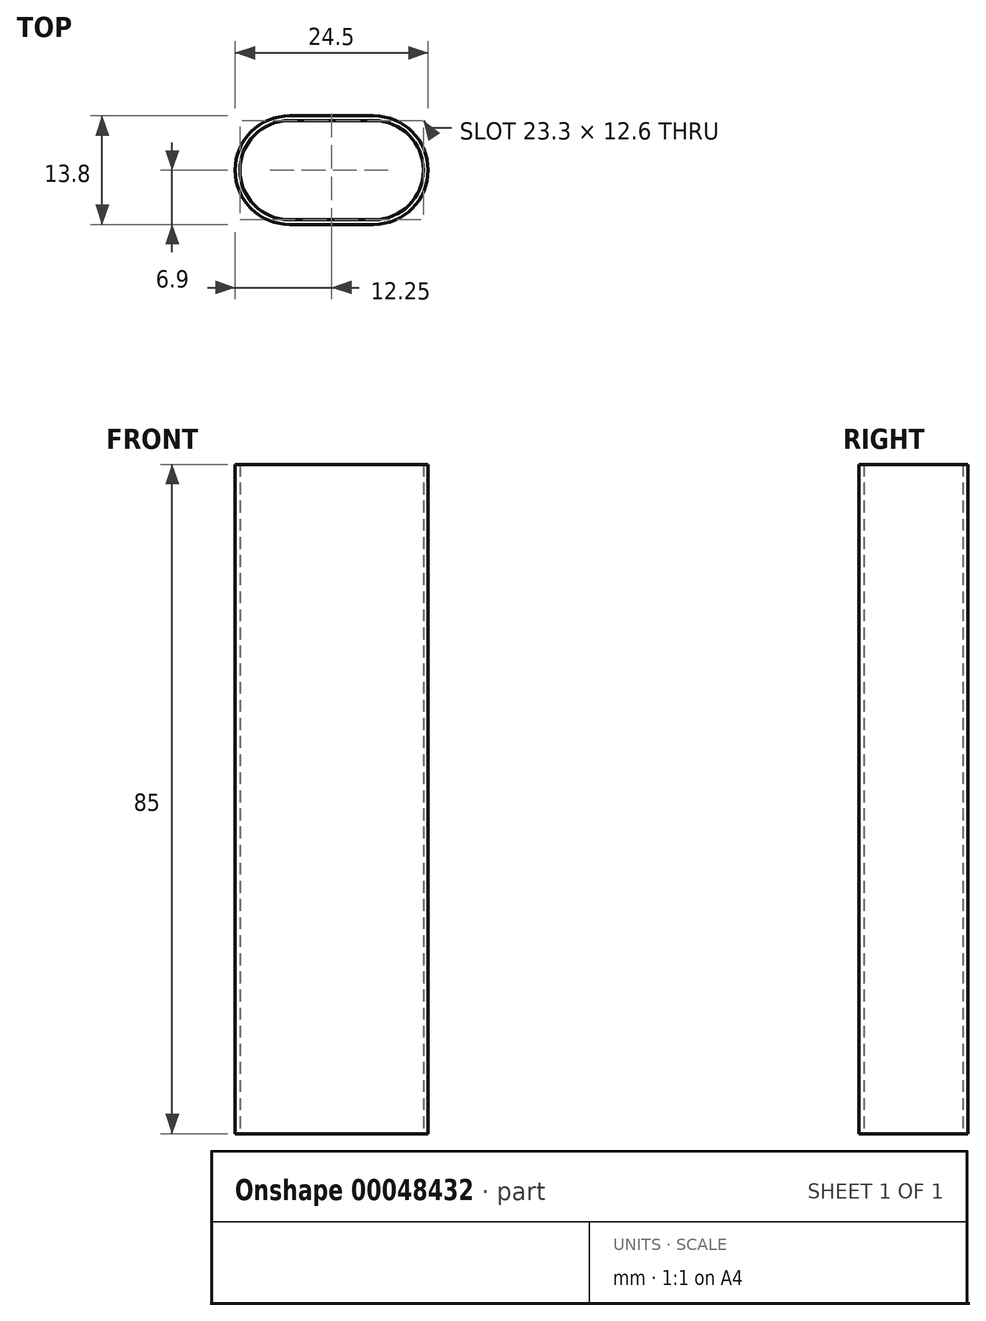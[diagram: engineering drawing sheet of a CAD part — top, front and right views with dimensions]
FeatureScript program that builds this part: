
annotation { "Feature Type Name" : "Feature", "Feature Type Description" : "" }
export const myFeature = defineFeature(function(context is Context, id is Id, definition is map)
    precondition{}
    {
        {
            var Q0;
            Q0=qCreatedBy(makeId("Top.planeOp"),FACE);
            var sketch = newSketch(context, id + "F0", { "sketchPlane" : qUnion([Q0])});
            skArc(sketch, "E0", {"start": v(-5.35, 6.9) * mm, "mid": v(-12.25, 0) * mm, "end": v(-5.35, -6.9) * mm});
            skArc(sketch, "E1.MirrorC", {"start": v(5.35, 6.9) * mm, "mid": v(12.25, 0) * mm, "end": v(5.35, -6.9) * mm});
            skLineSegment(sketch, "E2", {"start": v(-5.35, 6.9) * mm, "end": v(5.35, 6.9) * mm});
            skLineSegment(sketch, "E3.MirrorCS", {"start": v(-5.35, -6.9) * mm, "end": v(5.35, -6.9) * mm});
            skLineSegment(sketch, "E4.0", {"start": v(-5.35, 6.3) * mm, "end": v(5.35, 6.3) * mm});
            skArc(sketch, "E4.1", {"start": v(-5.35, 6.3) * mm, "mid": v(-11.65, 0) * mm, "end": v(-5.35, -6.3) * mm});
            skLineSegment(sketch, "E4.2", {"start": v(-5.35, -6.3) * mm, "end": v(5.35, -6.3) * mm});
            skArc(sketch, "E4.3", {"start": v(5.35, 6.3) * mm, "mid": v(11.65, 0) * mm, "end": v(5.35, -6.3) * mm});
            skLineSegment(sketch, "E5", {"start": v(-25, -20) * mm, "end": v(25, -20) * mm});
            skLineSegment(sketch, "E6", {"start": v(-25, -20) * mm, "end": v(-25, -27) * mm});
            skLineSegment(sketch, "E7", {"start": v(-25, -27) * mm, "end": v(25, -27) * mm});
            skLineSegment(sketch, "E8", {"start": v(25, -27) * mm, "end": v(25, -20) * mm});
            skSolve(sketch);
        }
        {
            var Q0;
            Q0 = qSketchRegion(id + "F0", true);
            extrude(context, id + "F1", {"entities" : qUnion([Q0]), "depth" : 85 * mm});
        }
        {
            var Q0;
            Q0=qCreatedBy(makeId("Right.planeOp"),FACE);
            var sketch = newSketch(context, id + "F2", { "sketchPlane" : qUnion([Q0])});
            skCircle(sketch, "E9", {"center": v(-35, 30) * mm, "radius": 12.5 * mm});
            skCircle(sketch, "E10", {"center": v(-35, 30) * mm, "radius": 7.5 * mm});
            skSolve(sketch);
        }
        {
            var Q0;
            Q0=makeQuery(id+"F2.imprint","IMPRINT",FACE,{"disambiguationData":[TD([[makeQuery(id+"F2.imprint","IMPRINT",EDGE,{"derivedFrom":sQuery(id+"F2.wireOp",EDGE,"E9")}),1.0]])]});
            extrude(context, id + "F3", {"entities" : qUnion([Q0]), "endBound" : BoundingType.SYMMETRIC, "depth" : 25 * mm});
        }
        {
            var Q0;
            Q0=makeQuery(id+"F3.opExtrude","CAP_FACE",FACE,{"disambiguationData":[OSD([sQuery(id+"F2.wireOp",EDGE,"E9"),sQuery(id+"F2.wireOp",EDGE,"E10")])],"isStart":false});
            var sketch = newSketch(context, id + "F4", { "sketchPlane" : qUnion([Q0])});
            skLineSegment(sketch, "E11.bottom", {"start": v(-55.62, 44.4) * mm, "end": v(-30, 44.4) * mm});
            skLineSegment(sketch, "E11.top", {"start": v(-55.62, 24.4) * mm, "end": v(-30, 24.4) * mm});
            skLineSegment(sketch, "E11.left", {"start": v(-55.62, 44.4) * mm, "end": v(-55.62, 24.4) * mm});
            skLineSegment(sketch, "E11.right", {"start": v(-30, 44.4) * mm, "end": v(-30, 24.4) * mm});
            skSolve(sketch);
        }
        {
            var Q0;
            Q0 = qSketchRegion(id + "F4", true);
            extrude(context, id + "F5", {"entities" : qUnion([Q0]), "operationType" : NewBodyOperationType.ADD, "depth" : 25 * mm});
        }
        {
            var Q0;
            Q0=makeQuery(id+"F3.opExtrude","SWEPT_BODY",BODY,{"disambiguationData":[OSD([sQuery(id+"F2.wireOp",EDGE,"E9"),sQuery(id+"F2.wireOp",EDGE,"E10")])]});
            var Q1;
            Q1=makeQuery(id+"F1.opExtrude","SWEPT_BODY",BODY,{"disambiguationData":[OSD([sQuery(id+"F0.wireOp",EDGE,"E5"),sQuery(id+"F0.wireOp",EDGE,"E6"),sQuery(id+"F0.wireOp",EDGE,"E7"),sQuery(id+"F0.wireOp",EDGE,"E8")])]});
            deleteBodies(context, id + "F6", {"entities" : qUnion([Q0, Q1])});
        }
    });
